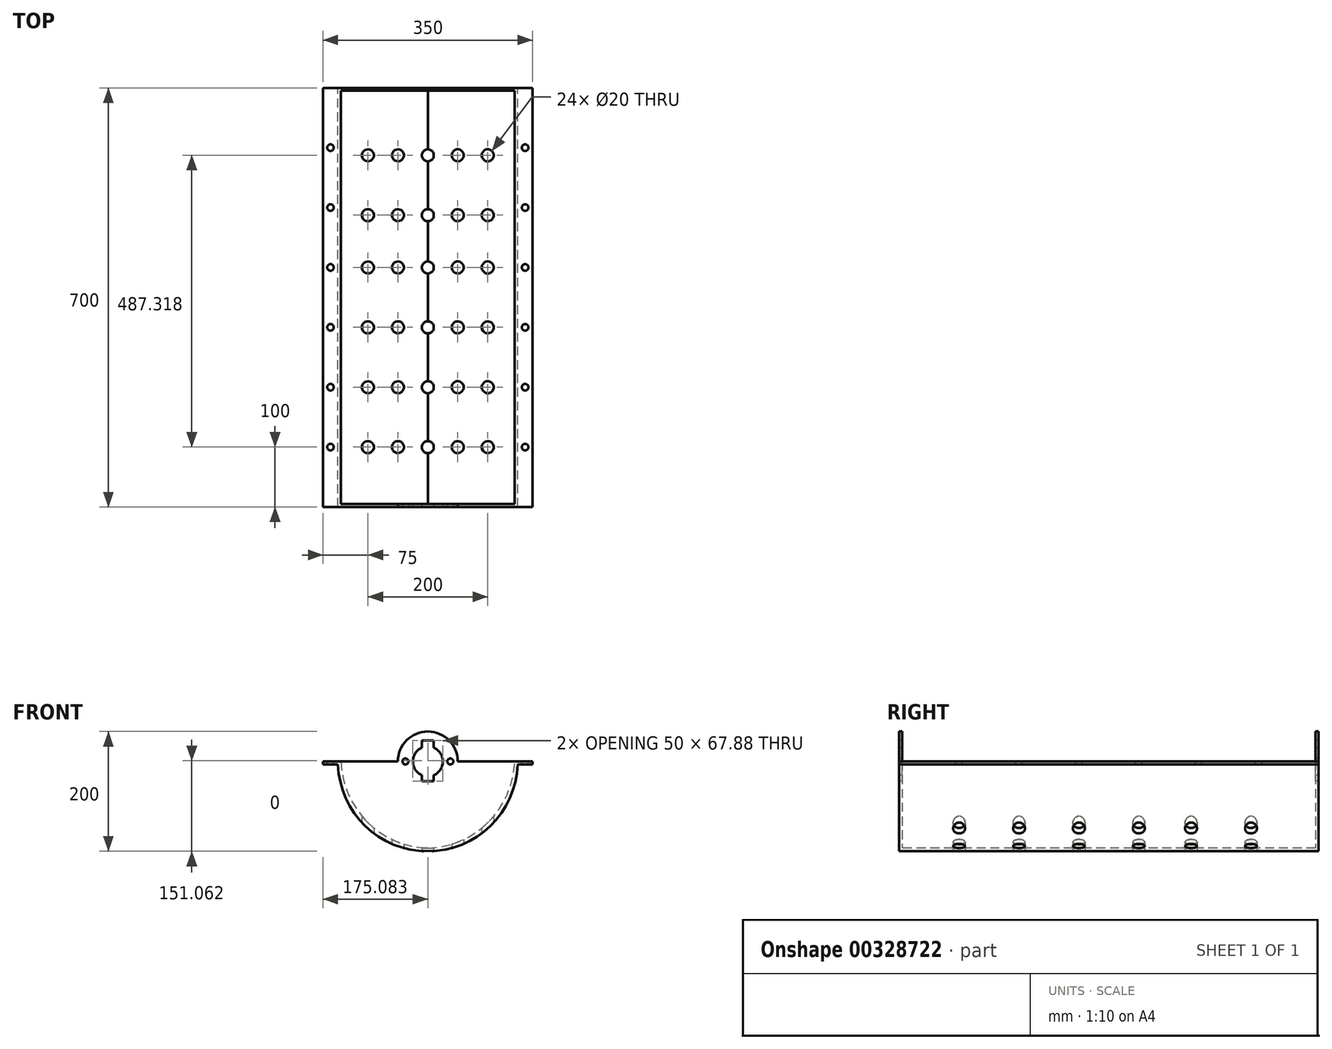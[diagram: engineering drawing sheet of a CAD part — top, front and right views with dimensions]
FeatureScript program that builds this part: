
annotation { "Feature Type Name" : "Feature", "Feature Type Description" : "" }
export const myFeature = defineFeature(function(context is Context, id is Id, definition is map)
    precondition{}
    {
        {
            var Q0;
            Q0=qCreatedBy(makeId("Front.planeOp"),FACE);
            var sketch = newSketch(context, id + "F0", { "sketchPlane" : qUnion([Q0])});
            skLineSegment(sketch, "E0.bottom", {"start": v(150, -75) * mm, "end": v(-150, -75) * mm});
            skLineSegment(sketch, "E0.top", {"start": v(150, 75) * mm, "end": v(-150, 75) * mm});
            skLineSegment(sketch, "E0.left", {"start": v(150, -75) * mm, "end": v(150, 70) * mm});
            skLineSegment(sketch, "E0.right", {"start": v(-150, -75) * mm, "end": v(-150, 70) * mm});
            skPoint(sketch, "E0.middle", {"position": v(0, 0) * mm});
            skLineSegment(sketch, "E1", {"start": v(-150, 75) * mm, "end": v(-175, 75) * mm});
            skLineSegment(sketch, "E2", {"start": v(-175, 75) * mm, "end": v(-175, 70) * mm});
            skLineSegment(sketch, "E3", {"start": v(-175, 70) * mm, "end": v(-150, 70) * mm});
            skLineSegment(sketch, "E4", {"start": v(150, 75) * mm, "end": v(175, 75) * mm});
            skLineSegment(sketch, "E5", {"start": v(175, 75) * mm, "end": v(175, 70) * mm});
            skLineSegment(sketch, "E6", {"start": v(175, 70) * mm, "end": v(150, 70) * mm});
            skLineSegment(sketch, "E7.bottom", {"start": v(50, 125) * mm, "end": v(-50, 125) * mm});
            skLineSegment(sketch, "E7.left", {"start": v(50, 125) * mm, "end": v(50, 75) * mm});
            skLineSegment(sketch, "E7.right", {"start": v(-50, 125) * mm, "end": v(-50, 75) * mm});
            skPoint(sketch, "E7.middle", {"position": v(0, 75) * mm});
            skPoint(sketch, "E8.orphan", {"position": v(50, 25) * mm});
            skPoint(sketch, "E9.orphan", {"position": v(-50, 25) * mm});
            skSolve(sketch);
        }
        {
            var Q0;
            Q0 = qSketchRegion(id + "F0", true);
            extrude(context, id + "F1", {"entities" : qUnion([Q0]), "depth" : 700 * mm});
        }
        {
            var Q0;
            Q0=makeQuery(id+"F1.opExtrude","SWEPT_FACE",FACE,{"disambiguationData":[OSD([sQuery(id+"F0.wireOp",EDGE,"E7.bottom")])]});
            var sketch = newSketch(context, id + "F2", { "sketchPlane" : qUnion([Q0])});
            skLineSegment(sketch, "E10.bottom", {"start": v(50, -695) * mm, "end": v(-50, -695) * mm});
            skLineSegment(sketch, "E10.top", {"start": v(50, -5) * mm, "end": v(-50, -5) * mm});
            skLineSegment(sketch, "E10.left", {"start": v(50, -695) * mm, "end": v(50, -5) * mm});
            skLineSegment(sketch, "E10.right", {"start": v(-50, -695) * mm, "end": v(-50, -5) * mm});
            skPoint(sketch, "E10.middle", {"position": v(0, -350) * mm});
            skPoint(sketch, "E10.middle.positionSnap0", {"position": v(0, -700) * mm});
            skPoint(sketch, "E10.middle.positionSnap1", {"position": v(50, -350) * mm});
            skPoint(sketch, "E10.centerSnap0", {"position": v(0, -700) * mm});
            skPoint(sketch, "E10.centerSnap1", {"position": v(50, -350) * mm});
            skSolve(sketch);
        }
        {
            var Q0;
            Q0=makeQuery(id+"F2.imprint","IMPRINT",FACE,{"disambiguationData":[TD([[makeQuery(id+"F2.imprint","IMPRINT",EDGE,{"derivedFrom":sQuery(id+"F2.wireOp",EDGE,"E10.bottom")}),-1.0]])]});
            extrude(context, id + "F3", {"entities" : qUnion([Q0]), "operationType" : NewBodyOperationType.REMOVE, "oppositeDirection" : true, "depth" : 50 * mm});
        }
        {
            var Q0;
            {var subQ0=sQuery(id+"F0.wireOp",EDGE,"E0.top");Q0=makeQuery(id+"F3.boolean.opBoolean","MERGE",FACE,{"derivedFrom":[makeQuery(id+"F1.opExtrude","SWEPT_FACE",FACE,{"disambiguationData":[OSD([subQ0,sQuery(id+"F0.wireOp",EDGE,"E4")])]}),makeQuery(id+"F1.opExtrude","SWEPT_FACE",FACE,{"disambiguationData":[OSD([subQ0,sQuery(id+"F0.wireOp",EDGE,"E1")])]}),makeQuery(id+"F3.opExtrude","CAP_FACE",FACE,{"disambiguationData":[OSD([sQuery(id+"F2.wireOp",EDGE,"E10.bottom"),sQuery(id+"F2.wireOp",EDGE,"E10.top"),sQuery(id+"F2.wireOp",EDGE,"E10.left"),sQuery(id+"F2.wireOp",EDGE,"E10.right")])],"isStart":false})]});}
            var sketch = newSketch(context, id + "F4", { "sketchPlane" : qUnion([Q0])});
            skLineSegment(sketch, "E11.bottom", {"start": v(145, -695) * mm, "end": v(-145, -695) * mm});
            skLineSegment(sketch, "E11.top", {"start": v(145, -5) * mm, "end": v(-145, -5) * mm});
            skLineSegment(sketch, "E11.left", {"start": v(145, -695) * mm, "end": v(145, -5) * mm});
            skLineSegment(sketch, "E11.right", {"start": v(-145, -695) * mm, "end": v(-145, -5) * mm});
            skPoint(sketch, "E11.middle", {"position": v(0, -350) * mm});
            skPoint(sketch, "E11.middle.positionSnap0", {"position": v(175, -350) * mm});
            skPoint(sketch, "E11.middle.positionSnap1", {"position": v(0, -5) * mm});
            skPoint(sketch, "E11.centerSnap0", {"position": v(175, -350) * mm});
            skPoint(sketch, "E11.centerSnap1", {"position": v(0, -5) * mm});
            skSolve(sketch);
        }
        {
            var Q0;
            Q0 = qSketchRegion(id + "F4", true);
            extrude(context, id + "F5", {"entities" : qUnion([Q0]), "operationType" : NewBodyOperationType.REMOVE, "oppositeDirection" : true, "depth" : 145 * mm});
        }
        {
            var Q0;
            Q0=makeQuery(id+"F1.opExtrude","SWEPT_FACE",FACE,{"disambiguationData":[OSD([sQuery(id+"F0.wireOp",EDGE,"E0.bottom")])]});
            var sketch = newSketch(context, id + "F6", { "sketchPlane" : qUnion([Q0])});
            skCircle(sketch, "E12", {"center": v(-100, 600) * mm, "radius": 10 * mm});
            skCircle(sketch, "E13", {"center": v(-50, 600) * mm, "radius": 10 * mm});
            skCircle(sketch, "E14", {"center": v(0, 600) * mm, "radius": 10 * mm});
            skCircle(sketch, "E15", {"center": v(50, 600) * mm, "radius": 10 * mm});
            skCircle(sketch, "E16", {"center": v(100, 600) * mm, "radius": 10 * mm});
            skCircle(sketch, "E17", {"center": v(100, 500) * mm, "radius": 10 * mm});
            skCircle(sketch, "E18", {"center": v(50, 500) * mm, "radius": 10 * mm});
            skCircle(sketch, "E19", {"center": v(0, 500) * mm, "radius": 10 * mm});
            skCircle(sketch, "E20", {"center": v(-50, 500) * mm, "radius": 10 * mm});
            skCircle(sketch, "E21", {"center": v(-100, 500) * mm, "radius": 10 * mm});
            skCircle(sketch, "E22", {"center": v(-100, 400) * mm, "radius": 10 * mm});
            skCircle(sketch, "E23", {"center": v(-50, 400) * mm, "radius": 10 * mm});
            skCircle(sketch, "E24", {"center": v(0, 400) * mm, "radius": 10 * mm});
            skCircle(sketch, "E25", {"center": v(50, 400) * mm, "radius": 10 * mm});
            skCircle(sketch, "E26", {"center": v(100, 400) * mm, "radius": 10 * mm});
            skCircle(sketch, "E27", {"center": v(-100, 300) * mm, "radius": 10 * mm});
            skCircle(sketch, "E28", {"center": v(-50, 300) * mm, "radius": 10 * mm});
            skCircle(sketch, "E29", {"center": v(0, 300) * mm, "radius": 10 * mm});
            skCircle(sketch, "E30", {"center": v(50, 300) * mm, "radius": 10 * mm});
            skCircle(sketch, "E31", {"center": v(100, 300) * mm, "radius": 10 * mm});
            skCircle(sketch, "E32", {"center": v(100, 212.68) * mm, "radius": 10 * mm});
            skCircle(sketch, "E33", {"center": v(50, 212.68) * mm, "radius": 10 * mm});
            skCircle(sketch, "E34", {"center": v(0, 212.68) * mm, "radius": 10 * mm});
            skCircle(sketch, "E35", {"center": v(-50, 212.68) * mm, "radius": 10 * mm});
            skCircle(sketch, "E36", {"center": v(-100, 212.68) * mm, "radius": 10 * mm});
            skCircle(sketch, "E37", {"center": v(-100, 112.68) * mm, "radius": 10 * mm});
            skCircle(sketch, "E38", {"center": v(-50, 112.68) * mm, "radius": 10 * mm});
            skCircle(sketch, "E39", {"center": v(0, 112.68) * mm, "radius": 10 * mm});
            skCircle(sketch, "E40", {"center": v(50, 112.68) * mm, "radius": 10 * mm});
            skCircle(sketch, "E41", {"center": v(100, 112.68) * mm, "radius": 10 * mm});
            skSolve(sketch);
        }
        {
            var Q0;
            Q0=makeQuery(id+"F5.boolean.opBoolean","COPY",EDGE,{"derivedFrom":makeQuery(id+"F5.opExtrude","CAP_EDGE",EDGE,{"disambiguationData":[OSD([sQuery(id+"F4.wireOp",EDGE,"E11.left")])],"isStart":false})});
            var Q1;
            Q1=makeQuery(id+"F5.boolean.opBoolean","COPY",EDGE,{"derivedFrom":makeQuery(id+"F5.opExtrude","CAP_EDGE",EDGE,{"disambiguationData":[OSD([sQuery(id+"F4.wireOp",EDGE,"E11.right")])],"isStart":false})});
            var Q2;
            Q2=makeQuery(id+"F1.opExtrude","SWEPT_EDGE",EDGE,{"disambiguationData":[OSD([sQuery(id+"F0.wireOp",EDGE,"E0.bottom"),sQuery(id+"F0.wireOp",EDGE,"E0.left")])]});
            var Q3;
            Q3=makeQuery(id+"F1.opExtrude","SWEPT_EDGE",EDGE,{"disambiguationData":[OSD([sQuery(id+"F0.wireOp",EDGE,"E0.bottom"),sQuery(id+"F0.wireOp",EDGE,"E0.right")])]});
            fillet(context, id + "F7", {"entities" : qUnion([Q0, Q1, Q2, Q3]), "radius" : 150 * mm, "tangentPropagation" : true, "allowEdgeOverflow" : false});
        }
        {
            var Q0;
            Q0=sQuery(id+"F6.wireOp",VERTEX,"E12.center");
            var Q1;
            Q1=sQuery(id+"F6.wireOp",VERTEX,"E13.center");
            var Q2;
            Q2=sQuery(id+"F6.wireOp",VERTEX,"E14.center");
            var Q3;
            Q3=sQuery(id+"F6.wireOp",VERTEX,"E15.center");
            var Q4;
            Q4=sQuery(id+"F6.wireOp",VERTEX,"E16.center");
            var Q5;
            Q5=sQuery(id+"F6.wireOp",VERTEX,"E17.center");
            var Q6;
            Q6=sQuery(id+"F6.wireOp",VERTEX,"E18.center");
            var Q7;
            Q7=sQuery(id+"F6.wireOp",VERTEX,"E19.center");
            var Q8;
            Q8=sQuery(id+"F6.wireOp",VERTEX,"E20.center");
            var Q9;
            Q9=sQuery(id+"F6.wireOp",VERTEX,"E21.center");
            var Q10;
            Q10=sQuery(id+"F6.wireOp",VERTEX,"E22.center");
            var Q11;
            Q11=sQuery(id+"F6.wireOp",VERTEX,"E23.center");
            var Q12;
            Q12=sQuery(id+"F6.wireOp",VERTEX,"E24.center");
            var Q13;
            Q13=sQuery(id+"F6.wireOp",VERTEX,"E25.center");
            var Q14;
            Q14=sQuery(id+"F6.wireOp",VERTEX,"E26.center");
            var Q15;
            Q15=sQuery(id+"F6.wireOp",VERTEX,"E31.center");
            var Q16;
            Q16=sQuery(id+"F6.wireOp",VERTEX,"E30.center");
            var Q17;
            Q17=sQuery(id+"F6.wireOp",VERTEX,"E29.center");
            var Q18;
            Q18=sQuery(id+"F6.wireOp",VERTEX,"E28.center");
            var Q19;
            Q19=sQuery(id+"F6.wireOp",VERTEX,"E27.center");
            var Q20;
            Q20=sQuery(id+"F6.wireOp",VERTEX,"E36.center");
            var Q21;
            Q21=sQuery(id+"F6.wireOp",VERTEX,"E35.center");
            var Q22;
            Q22=sQuery(id+"F6.wireOp",VERTEX,"E34.center");
            var Q23;
            Q23=sQuery(id+"F6.wireOp",VERTEX,"E32.center");
            var Q24;
            Q24=sQuery(id+"F6.wireOp",VERTEX,"E33.center");
            var Q25;
            Q25=sQuery(id+"F6.wireOp",VERTEX,"E35.center");
            var Q26;
            Q26=sQuery(id+"F6.wireOp",VERTEX,"E37.center");
            var Q27;
            Q27=sQuery(id+"F6.wireOp",VERTEX,"E38.center");
            var Q28;
            Q28=sQuery(id+"F6.wireOp",VERTEX,"E39.center");
            var Q29;
            Q29=sQuery(id+"F6.wireOp",VERTEX,"E41.center");
            var Q30;
            Q30=sQuery(id+"F6.wireOp",VERTEX,"E40.center");
            var Q31;
            Q31=makeQuery(id+"F1.opExtrude","SWEPT_BODY",BODY,{"disambiguationData":[OSD([sQuery(id+"F0.wireOp",EDGE,"E0.bottom"),sQuery(id+"F0.wireOp",EDGE,"E0.top"),sQuery(id+"F0.wireOp",EDGE,"E0.left"),sQuery(id+"F0.wireOp",EDGE,"E0.right"),sQuery(id+"F0.wireOp",EDGE,"E1"),sQuery(id+"F0.wireOp",EDGE,"E2"),sQuery(id+"F0.wireOp",EDGE,"E3"),sQuery(id+"F0.wireOp",EDGE,"E4"),sQuery(id+"F0.wireOp",EDGE,"E5"),sQuery(id+"F0.wireOp",EDGE,"E6"),sQuery(id+"F0.wireOp",EDGE,"E7.bottom"),sQuery(id+"F0.wireOp",EDGE,"E7.left"),sQuery(id+"F0.wireOp",EDGE,"E7.right")])]});
            hole(context, id + "F8", {"style" : HoleStyle.SIMPLE, "endStyle" : HoleEndStyle.THROUGH, "holeDiameter" : 20 * mm, "isTappedThrough" : true, "tappedDepth" : 14 * mm, "tapClearance" : 3, "locations" : qUnion([Q0, Q1, Q2, Q3, Q4, Q5, Q6, Q7, Q8, Q9, Q10, Q11, Q12, Q13, Q14, Q15, Q16, Q17, Q18, Q19, Q20, Q21, Q22, Q23, Q24, Q25, Q26, Q27, Q28, Q29, Q30]), "scope" : qUnion([Q31])});
        }
        {
            var Q0;
            {var subQ0=sQuery(id+"F0.wireOp",EDGE,"E7.left");var subQ1=sQuery(id+"F0.wireOp",EDGE,"E7.bottom");Q0=makeQuery(id+"F3.boolean.opBoolean","SPLIT",EDGE,{"disambiguationData":[TD([makeQuery(id+"F3.opExtrude","SWEPT_FACE",FACE,{"disambiguationData":[OSD([sQuery(id+"F2.wireOp",EDGE,"E10.bottom")])]})])],"derivedFrom":makeQuery(id+"F1.opExtrude","SWEPT_EDGE",EDGE,{"disambiguationData":[OSD([subQ1,subQ0])]})});}
            var Q1;
            {var subQ0=sQuery(id+"F0.wireOp",EDGE,"E7.right");var subQ1=sQuery(id+"F0.wireOp",EDGE,"E7.bottom");Q1=makeQuery(id+"F3.boolean.opBoolean","SPLIT",EDGE,{"disambiguationData":[TD([makeQuery(id+"F3.opExtrude","SWEPT_FACE",FACE,{"disambiguationData":[OSD([sQuery(id+"F2.wireOp",EDGE,"E10.bottom")])]})])],"derivedFrom":makeQuery(id+"F1.opExtrude","SWEPT_EDGE",EDGE,{"disambiguationData":[OSD([subQ1,subQ0])]})});}
            var Q2;
            {var subQ0=sQuery(id+"F0.wireOp",EDGE,"E7.left");var subQ1=sQuery(id+"F0.wireOp",EDGE,"E7.bottom");Q2=makeQuery(id+"F3.boolean.opBoolean","SPLIT",EDGE,{"disambiguationData":[TD([makeQuery(id+"F3.opExtrude","SWEPT_FACE",FACE,{"disambiguationData":[OSD([sQuery(id+"F2.wireOp",EDGE,"E10.top")])]})])],"derivedFrom":makeQuery(id+"F1.opExtrude","SWEPT_EDGE",EDGE,{"disambiguationData":[OSD([subQ1,subQ0])]})});}
            var Q3;
            {var subQ0=sQuery(id+"F0.wireOp",EDGE,"E7.right");var subQ1=sQuery(id+"F0.wireOp",EDGE,"E7.bottom");Q3=makeQuery(id+"F3.boolean.opBoolean","SPLIT",EDGE,{"disambiguationData":[TD([makeQuery(id+"F3.opExtrude","SWEPT_FACE",FACE,{"disambiguationData":[OSD([sQuery(id+"F2.wireOp",EDGE,"E10.top")])]})])],"derivedFrom":makeQuery(id+"F1.opExtrude","SWEPT_EDGE",EDGE,{"disambiguationData":[OSD([subQ1,subQ0])]})});}
            fillet(context, id + "F9", {"entities" : qUnion([Q0, Q1, Q2, Q3]), "radius" : 50 * mm, "tangentPropagation" : true, "allowEdgeOverflow" : false});
        }
        {
            var Q0;
            Q0=makeQuery(id+"F1.opExtrude","CAP_FACE",FACE,{"disambiguationData":[OSD([sQuery(id+"F0.wireOp",EDGE,"E0.bottom"),sQuery(id+"F0.wireOp",EDGE,"E0.top"),sQuery(id+"F0.wireOp",EDGE,"E0.left"),sQuery(id+"F0.wireOp",EDGE,"E0.right"),sQuery(id+"F0.wireOp",EDGE,"E1"),sQuery(id+"F0.wireOp",EDGE,"E2"),sQuery(id+"F0.wireOp",EDGE,"E3"),sQuery(id+"F0.wireOp",EDGE,"E4"),sQuery(id+"F0.wireOp",EDGE,"E5"),sQuery(id+"F0.wireOp",EDGE,"E6"),sQuery(id+"F0.wireOp",EDGE,"E7.bottom"),sQuery(id+"F0.wireOp",EDGE,"E7.left"),sQuery(id+"F0.wireOp",EDGE,"E7.right")])],"isStart":false});
            var sketch = newSketch(context, id + "F10", { "sketchPlane" : qUnion([Q0])});
            skArc(sketch, "E42", {"start": v(-10, 97.88) * mm, "mid": v(-24.92, 75) * mm, "end": v(-10, 52.12) * mm});
            skLineSegment(sketch, "E43", {"start": v(0, 110) * mm, "end": v(-10, 110) * mm});
            skLineSegment(sketch, "E44", {"start": v(-10, 110) * mm, "end": v(-10, 97.88) * mm});
            skLineSegment(sketch, "E45", {"start": v(0, 110) * mm, "end": v(10, 110) * mm});
            skLineSegment(sketch, "E46", {"start": v(10, 110) * mm, "end": v(10, 97.95) * mm});
            skLineSegment(sketch, "E47", {"start": v(-10, 52.12) * mm, "end": v(-10, 42.12) * mm});
            skLineSegment(sketch, "E48", {"start": v(-10, 42.12) * mm, "end": v(10, 42.12) * mm});
            skLineSegment(sketch, "E49", {"start": v(10, 42.12) * mm, "end": v(10, 52.05) * mm});
            skPoint(sketch, "E50.start.orphan", {"position": v(0, 100) * mm});
            skArc(sketch, "E51.trimOffspring", {"start": v(10, 52.05) * mm, "mid": v(25.08, 75) * mm, "end": v(10, 97.95) * mm});
            skCircle(sketch, "E52", {"center": v(-37.42, 75) * mm, "radius": 5 * mm});
            skCircle(sketch, "E53", {"center": v(37.58, 75) * mm, "radius": 5 * mm});
            skSolve(sketch);
        }
        {
            var Q0;
            Q0=makeQuery(id+"F10.imprint","IMPRINT",FACE,{"disambiguationData":[TD([[makeQuery(id+"F10.imprint","IMPRINT",EDGE,{"derivedFrom":sQuery(id+"F10.wireOp",EDGE,"E42")}),1.0]])]});
            extrude(context, id + "F11", {"entities" : qUnion([Q0]), "operationType" : NewBodyOperationType.REMOVE, "oppositeDirection" : true, "depth" : 700 * mm});
        }
        {
            var Q0;
            Q0=makeQuery(id+"F1.opExtrude","CAP_FACE",FACE,{"disambiguationData":[OSD([sQuery(id+"F0.wireOp",EDGE,"E0.bottom"),sQuery(id+"F0.wireOp",EDGE,"E0.top"),sQuery(id+"F0.wireOp",EDGE,"E0.left"),sQuery(id+"F0.wireOp",EDGE,"E0.right"),sQuery(id+"F0.wireOp",EDGE,"E1"),sQuery(id+"F0.wireOp",EDGE,"E2"),sQuery(id+"F0.wireOp",EDGE,"E3"),sQuery(id+"F0.wireOp",EDGE,"E4"),sQuery(id+"F0.wireOp",EDGE,"E5"),sQuery(id+"F0.wireOp",EDGE,"E6"),sQuery(id+"F0.wireOp",EDGE,"E7.bottom"),sQuery(id+"F0.wireOp",EDGE,"E7.left"),sQuery(id+"F0.wireOp",EDGE,"E7.right")])],"isStart":false});
            var sketch = newSketch(context, id + "F12", { "sketchPlane" : qUnion([Q0])});
            skCircle(sketch, "E54", {"center": v(37.58, 75) * mm, "radius": 5 * mm});
            skCircle(sketch, "E55", {"center": v(-37.42, 75) * mm, "radius": 5 * mm});
            skSolve(sketch);
        }
        {
            var Q0;
            Q0=sQuery(id+"F12.wireOp",VERTEX,"E55.center");
            var Q1;
            Q1=sQuery(id+"F12.wireOp",VERTEX,"E54.center");
            var Q2;
            Q2=makeQuery(id+"F1.opExtrude","SWEPT_BODY",BODY,{"disambiguationData":[OSD([sQuery(id+"F0.wireOp",EDGE,"E0.bottom"),sQuery(id+"F0.wireOp",EDGE,"E0.top"),sQuery(id+"F0.wireOp",EDGE,"E0.left"),sQuery(id+"F0.wireOp",EDGE,"E0.right"),sQuery(id+"F0.wireOp",EDGE,"E1"),sQuery(id+"F0.wireOp",EDGE,"E2"),sQuery(id+"F0.wireOp",EDGE,"E3"),sQuery(id+"F0.wireOp",EDGE,"E4"),sQuery(id+"F0.wireOp",EDGE,"E5"),sQuery(id+"F0.wireOp",EDGE,"E6"),sQuery(id+"F0.wireOp",EDGE,"E7.bottom"),sQuery(id+"F0.wireOp",EDGE,"E7.left"),sQuery(id+"F0.wireOp",EDGE,"E7.right")])]});
            hole(context, id + "F13", {"style" : HoleStyle.SIMPLE, "endStyle" : HoleEndStyle.THROUGH, "holeDiameter" : 10 * mm, "isTappedThrough" : true, "tappedDepth" : 14 * mm, "tapClearance" : 3, "locations" : qUnion([Q0, Q1]), "scope" : qUnion([Q2])});
        }
        {
            var Q0;
            {var subQ0=sQuery(id+"F0.wireOp",EDGE,"E5");var subQ5=sQuery(id+"F0.wireOp",EDGE,"E4");var subQ8=sQuery(id+"F0.wireOp",EDGE,"E1");var subQ11=sQuery(id+"F0.wireOp",EDGE,"E0.top");var subQ13=sQuery(id+"F2.wireOp",EDGE,"E10.bottom");var subQ14=sQuery(id+"F2.wireOp",EDGE,"E10.top");Q0=makeQuery(id+"F5.boolean.opBoolean","SPLIT",FACE,{"disambiguationData":[TD([makeQuery(id+"F1.opExtrude","SWEPT_FACE",FACE,{"disambiguationData":[OSD([subQ0])]})])],"derivedFrom":makeQuery(id+"F3.boolean.opBoolean","MERGE",FACE,{"derivedFrom":[makeQuery(id+"F1.opExtrude","SWEPT_FACE",FACE,{"disambiguationData":[OSD([subQ11,subQ5])]}),makeQuery(id+"F1.opExtrude","SWEPT_FACE",FACE,{"disambiguationData":[OSD([subQ11,subQ8])]}),makeQuery(id+"F3.opExtrude","CAP_FACE",FACE,{"disambiguationData":[OSD([subQ13,subQ14,sQuery(id+"F2.wireOp",EDGE,"E10.left"),sQuery(id+"F2.wireOp",EDGE,"E10.right")])],"isStart":false})]})});}
            var sketch = newSketch(context, id + "F14", { "sketchPlane" : qUnion([Q0])});
            skCircle(sketch, "E56", {"center": v(162.5, -100) * mm, "radius": 5 * mm});
            skCircle(sketch, "E57", {"center": v(162.5, -400) * mm, "radius": 5 * mm});
            skCircle(sketch, "E58", {"center": v(162.5, -500) * mm, "radius": 5 * mm});
            skCircle(sketch, "E59", {"center": v(162.5, -600) * mm, "radius": 5 * mm});
            skCircle(sketch, "E60", {"center": v(162.5, -200) * mm, "radius": 5 * mm});
            skCircle(sketch, "E61", {"center": v(162.5, -300) * mm, "radius": 5 * mm});
            skSolve(sketch);
        }
        {
            var Q0;
            Q0=sQuery(id+"F14.wireOp",VERTEX,"E56.center");
            var Q1;
            Q1=sQuery(id+"F14.wireOp",VERTEX,"E60.center");
            var Q2;
            Q2=sQuery(id+"F14.wireOp",VERTEX,"E61.center");
            var Q3;
            Q3=sQuery(id+"F14.wireOp",VERTEX,"E57.center");
            var Q4;
            Q4=sQuery(id+"F14.wireOp",VERTEX,"E58.center");
            var Q5;
            Q5=sQuery(id+"F14.wireOp",VERTEX,"E59.center");
            var Q6;
            Q6=makeQuery(id+"F1.opExtrude","SWEPT_BODY",BODY,{"disambiguationData":[OSD([sQuery(id+"F0.wireOp",EDGE,"E0.bottom"),sQuery(id+"F0.wireOp",EDGE,"E0.top"),sQuery(id+"F0.wireOp",EDGE,"E0.left"),sQuery(id+"F0.wireOp",EDGE,"E0.right"),sQuery(id+"F0.wireOp",EDGE,"E1"),sQuery(id+"F0.wireOp",EDGE,"E2"),sQuery(id+"F0.wireOp",EDGE,"E3"),sQuery(id+"F0.wireOp",EDGE,"E4"),sQuery(id+"F0.wireOp",EDGE,"E5"),sQuery(id+"F0.wireOp",EDGE,"E6"),sQuery(id+"F0.wireOp",EDGE,"E7.bottom"),sQuery(id+"F0.wireOp",EDGE,"E7.left"),sQuery(id+"F0.wireOp",EDGE,"E7.right")])]});
            hole(context, id + "F15", {"style" : HoleStyle.SIMPLE, "endStyle" : HoleEndStyle.THROUGH, "standardTappedOrClearance" : lookupTablePath({ "standard" : "ISO", "fit" : "Normal", "size" : "M10", "type" : "Clearance" }), "standardBlindInLast" : lookupTablePath({ "fit" : "Standard", "standard" : "ISO", "size" : "M10", "type" : "Clearance" }), "holeDiameter" : 11 * mm, "isTappedThrough" : true, "tappedDepth" : 14 * mm, "tapClearance" : 3, "locations" : qUnion([Q0, Q1, Q2, Q3, Q4, Q5]), "scope" : qUnion([Q6])});
        }
        {
            var Q0;
            {var subQ5=sQuery(id+"F0.wireOp",EDGE,"E4");var subQ7=sQuery(id+"F0.wireOp",EDGE,"E2");var subQ8=sQuery(id+"F0.wireOp",EDGE,"E1");var subQ11=sQuery(id+"F0.wireOp",EDGE,"E0.top");var subQ13=sQuery(id+"F2.wireOp",EDGE,"E10.top");var subQ14=sQuery(id+"F2.wireOp",EDGE,"E10.bottom");Q0=makeQuery(id+"F5.boolean.opBoolean","SPLIT",FACE,{"disambiguationData":[TD([makeQuery(id+"F1.opExtrude","SWEPT_FACE",FACE,{"disambiguationData":[OSD([subQ7])]})])],"derivedFrom":makeQuery(id+"F3.boolean.opBoolean","MERGE",FACE,{"derivedFrom":[makeQuery(id+"F1.opExtrude","SWEPT_FACE",FACE,{"disambiguationData":[OSD([subQ11,subQ5])]}),makeQuery(id+"F1.opExtrude","SWEPT_FACE",FACE,{"disambiguationData":[OSD([subQ11,subQ8])]}),makeQuery(id+"F3.opExtrude","CAP_FACE",FACE,{"disambiguationData":[OSD([subQ14,subQ13,sQuery(id+"F2.wireOp",EDGE,"E10.left"),sQuery(id+"F2.wireOp",EDGE,"E10.right")])],"isStart":false})]})});}
            var sketch = newSketch(context, id + "F16", { "sketchPlane" : qUnion([Q0])});
            skCircle(sketch, "E62", {"center": v(-162.5, -100) * mm, "radius": 5 * mm});
            skCircle(sketch, "E63", {"center": v(-162.5, -200) * mm, "radius": 5 * mm});
            skCircle(sketch, "E64", {"center": v(-162.5, -300) * mm, "radius": 5 * mm});
            skCircle(sketch, "E65", {"center": v(-162.5, -500) * mm, "radius": 5 * mm});
            skCircle(sketch, "E66", {"center": v(-162.5, -600) * mm, "radius": 5.9 * mm});
            skCircle(sketch, "E67", {"center": v(-162.5, -400) * mm, "radius": 5 * mm});
            skSolve(sketch);
        }
        {
            var Q0;
            Q0=sQuery(id+"F16.wireOp",VERTEX,"E62.center");
            var Q1;
            Q1=sQuery(id+"F16.wireOp",VERTEX,"E63.center");
            var Q2;
            Q2=sQuery(id+"F16.wireOp",VERTEX,"E64.center");
            var Q3;
            Q3=sQuery(id+"F16.wireOp",VERTEX,"E67.center");
            var Q4;
            Q4=sQuery(id+"F16.wireOp",VERTEX,"E65.center");
            var Q5;
            Q5=sQuery(id+"F16.wireOp",VERTEX,"E66.center");
            var Q6;
            Q6=makeQuery(id+"F1.opExtrude","SWEPT_BODY",BODY,{"disambiguationData":[OSD([sQuery(id+"F0.wireOp",EDGE,"E0.bottom"),sQuery(id+"F0.wireOp",EDGE,"E0.top"),sQuery(id+"F0.wireOp",EDGE,"E0.left"),sQuery(id+"F0.wireOp",EDGE,"E0.right"),sQuery(id+"F0.wireOp",EDGE,"E1"),sQuery(id+"F0.wireOp",EDGE,"E2"),sQuery(id+"F0.wireOp",EDGE,"E3"),sQuery(id+"F0.wireOp",EDGE,"E4"),sQuery(id+"F0.wireOp",EDGE,"E5"),sQuery(id+"F0.wireOp",EDGE,"E6"),sQuery(id+"F0.wireOp",EDGE,"E7.bottom"),sQuery(id+"F0.wireOp",EDGE,"E7.left"),sQuery(id+"F0.wireOp",EDGE,"E7.right")])]});
            hole(context, id + "F17", {"style" : HoleStyle.SIMPLE, "endStyle" : HoleEndStyle.THROUGH, "standardTappedOrClearance" : lookupTablePath({ "standard" : "ISO", "fit" : "Normal", "size" : "M10", "type" : "Clearance" }), "standardBlindInLast" : lookupTablePath({ "fit" : "Standard", "standard" : "ISO", "size" : "M10", "type" : "Clearance" }), "holeDiameter" : 11 * mm, "isTappedThrough" : true, "tappedDepth" : 14 * mm, "tapClearance" : 3, "locations" : qUnion([Q0, Q1, Q2, Q3, Q4, Q5]), "scope" : qUnion([Q6])});
        }
    });
